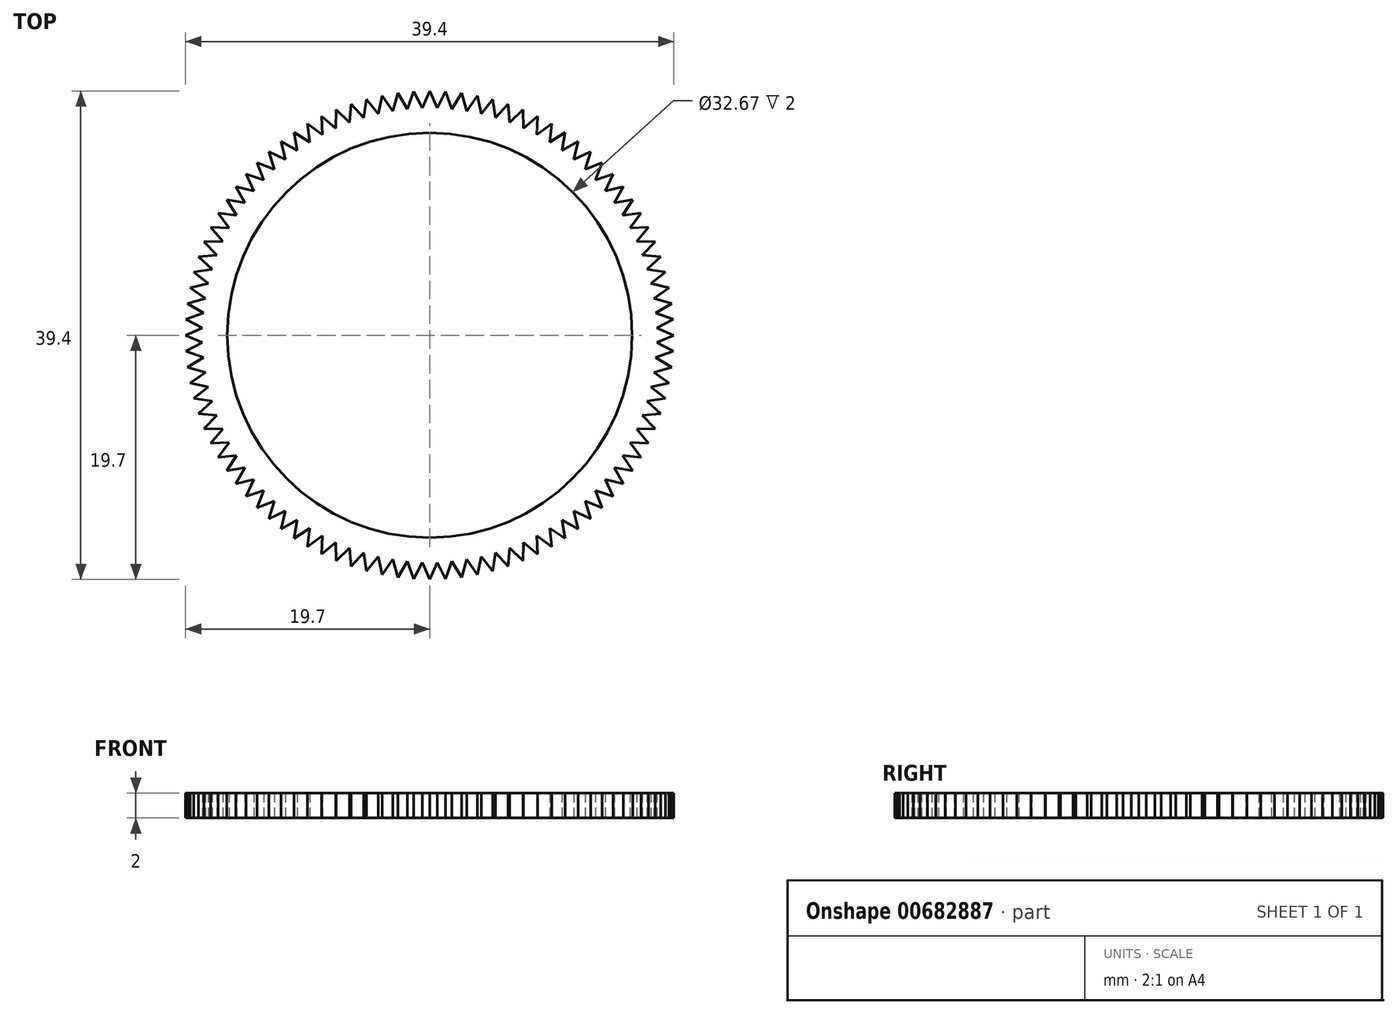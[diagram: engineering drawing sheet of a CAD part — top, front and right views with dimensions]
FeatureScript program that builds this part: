
annotation { "Feature Type Name" : "Feature", "Feature Type Description" : "" }
export const myFeature = defineFeature(function(context is Context, id is Id, definition is map)
    precondition{}
    {
        {
            var Q0;
            Q0=qCreatedBy(makeId("Top.planeOp"),FACE);
            var sketch = newSketch(context, id + "F0", { "sketchPlane" : qUnion([Q0])});
            skLineSegment(sketch, "E0", {"start": v(0, 19.7) * mm, "end": v(0.6, 18.33) * mm});
            skLineSegment(sketch, "E1.MirrorCS", {"start": v(0, 19.7) * mm, "end": v(-0.6, 18.33) * mm});
            skLineSegment(sketch, "E2.1.0", {"start": v(-1.29, 19.66) * mm, "end": v(-1.8, 18.25) * mm});
            skLineSegment(sketch, "E2.1.1", {"start": v(-1.29, 19.66) * mm, "end": v(-0.6, 18.33) * mm});
            skLineSegment(sketch, "E2.2.0", {"start": v(-2.57, 19.53) * mm, "end": v(-2.99, 18.1) * mm});
            skLineSegment(sketch, "E2.2.1", {"start": v(-2.57, 19.53) * mm, "end": v(-1.8, 18.25) * mm});
            skPoint(sketch, "E2.center", {"position": v(0, 0) * mm});
            skLineSegment(sketch, "E3.2.3.0", {"start": v(-3.84, 19.32) * mm, "end": v(-4.16, 17.86) * mm});
            skLineSegment(sketch, "E3.3.3.0", {"start": v(-3.84, 19.32) * mm, "end": v(-2.99, 18.1) * mm});
            skLineSegment(sketch, "E3.2.4.0", {"start": v(-5.1, 19.03) * mm, "end": v(-5.32, 17.55) * mm});
            skLineSegment(sketch, "E3.3.4.0", {"start": v(-5.1, 19.03) * mm, "end": v(-4.16, 17.86) * mm});
            skLineSegment(sketch, "E3.2.5.0", {"start": v(-6.33, 18.66) * mm, "end": v(-6.46, 17.16) * mm});
            skLineSegment(sketch, "E3.3.5.0", {"start": v(-6.33, 18.66) * mm, "end": v(-5.32, 17.55) * mm});
            skLineSegment(sketch, "E3.2.6.0", {"start": v(-7.54, 18.2) * mm, "end": v(-7.57, 16.7) * mm});
            skLineSegment(sketch, "E3.3.6.0", {"start": v(-7.54, 18.2) * mm, "end": v(-6.46, 17.16) * mm});
            skLineSegment(sketch, "E3.2.7.0", {"start": v(-8.71, 17.67) * mm, "end": v(-8.64, 16.17) * mm});
            skLineSegment(sketch, "E3.3.7.0", {"start": v(-8.71, 17.67) * mm, "end": v(-7.57, 16.7) * mm});
            skLineSegment(sketch, "E3.2.8.0", {"start": v(-9.85, 17.06) * mm, "end": v(-9.68, 15.57) * mm});
            skLineSegment(sketch, "E3.3.8.0", {"start": v(-9.85, 17.06) * mm, "end": v(-8.64, 16.17) * mm});
            skLineSegment(sketch, "E3.2.9.0", {"start": v(-10.95, 16.38) * mm, "end": v(-10.68, 14.9) * mm});
            skLineSegment(sketch, "E3.3.9.0", {"start": v(-10.95, 16.38) * mm, "end": v(-9.68, 15.57) * mm});
            skLineSegment(sketch, "E4.2.10.0", {"start": v(-12, 15.63) * mm, "end": v(-11.63, 14.18) * mm});
            skLineSegment(sketch, "E4.3.10.0", {"start": v(-12, 15.63) * mm, "end": v(-10.68, 14.9) * mm});
            skLineSegment(sketch, "E4.2.11.0", {"start": v(-13, 14.81) * mm, "end": v(-12.54, 13.38) * mm});
            skLineSegment(sketch, "E4.3.11.0", {"start": v(-13, 14.81) * mm, "end": v(-11.63, 14.18) * mm});
            skLineSegment(sketch, "E4.2.12.0", {"start": v(-13.93, 13.93) * mm, "end": v(-13.38, 12.54) * mm});
            skLineSegment(sketch, "E4.3.12.0", {"start": v(-13.93, 13.93) * mm, "end": v(-12.54, 13.38) * mm});
            skLineSegment(sketch, "E4.2.13.0", {"start": v(-14.81, 13) * mm, "end": v(-14.18, 11.63) * mm});
            skLineSegment(sketch, "E4.3.13.0", {"start": v(-14.81, 13) * mm, "end": v(-13.38, 12.54) * mm});
            skLineSegment(sketch, "E4.2.14.0", {"start": v(-15.63, 12) * mm, "end": v(-14.9, 10.68) * mm});
            skLineSegment(sketch, "E4.3.14.0", {"start": v(-15.63, 12) * mm, "end": v(-14.18, 11.63) * mm});
            skLineSegment(sketch, "E4.2.15.0", {"start": v(-16.38, 10.95) * mm, "end": v(-15.57, 9.68) * mm});
            skLineSegment(sketch, "E4.3.15.0", {"start": v(-16.38, 10.95) * mm, "end": v(-14.9, 10.68) * mm});
            skLineSegment(sketch, "E4.2.16.0", {"start": v(-17.06, 9.85) * mm, "end": v(-16.17, 8.64) * mm});
            skLineSegment(sketch, "E4.3.16.0", {"start": v(-17.06, 9.85) * mm, "end": v(-15.57, 9.68) * mm});
            skLineSegment(sketch, "E4.2.17.0", {"start": v(-17.67, 8.71) * mm, "end": v(-16.7, 7.57) * mm});
            skLineSegment(sketch, "E4.3.17.0", {"start": v(-17.67, 8.71) * mm, "end": v(-16.17, 8.64) * mm});
            skLineSegment(sketch, "E4.2.18.0", {"start": v(-18.2, 7.54) * mm, "end": v(-17.16, 6.46) * mm});
            skLineSegment(sketch, "E4.3.18.0", {"start": v(-18.2, 7.54) * mm, "end": v(-16.7, 7.57) * mm});
            skLineSegment(sketch, "E4.2.19.0", {"start": v(-18.66, 6.33) * mm, "end": v(-17.55, 5.32) * mm});
            skLineSegment(sketch, "E4.3.19.0", {"start": v(-18.66, 6.33) * mm, "end": v(-17.16, 6.46) * mm});
            skLineSegment(sketch, "E4.2.20.0", {"start": v(-19.03, 5.1) * mm, "end": v(-17.86, 4.16) * mm});
            skLineSegment(sketch, "E4.3.20.0", {"start": v(-19.03, 5.1) * mm, "end": v(-17.55, 5.32) * mm});
            skLineSegment(sketch, "E4.2.21.0", {"start": v(-19.32, 3.84) * mm, "end": v(-18.1, 2.99) * mm});
            skLineSegment(sketch, "E4.3.21.0", {"start": v(-19.32, 3.84) * mm, "end": v(-17.86, 4.16) * mm});
            skLineSegment(sketch, "E4.2.22.0", {"start": v(-19.53, 2.57) * mm, "end": v(-18.25, 1.8) * mm});
            skLineSegment(sketch, "E4.3.22.0", {"start": v(-19.53, 2.57) * mm, "end": v(-18.1, 2.99) * mm});
            skLineSegment(sketch, "E4.2.23.0", {"start": v(-19.66, 1.29) * mm, "end": v(-18.33, 0.6) * mm});
            skLineSegment(sketch, "E4.3.23.0", {"start": v(-19.66, 1.29) * mm, "end": v(-18.25, 1.8) * mm});
            skLineSegment(sketch, "E4.2.24.0", {"start": v(-19.7, 0) * mm, "end": v(-18.33, -0.6) * mm});
            skLineSegment(sketch, "E4.3.24.0", {"start": v(-19.7, 0) * mm, "end": v(-18.33, 0.6) * mm});
            skLineSegment(sketch, "E4.2.25.0", {"start": v(-19.66, -1.29) * mm, "end": v(-18.25, -1.8) * mm});
            skLineSegment(sketch, "E4.3.25.0", {"start": v(-19.66, -1.29) * mm, "end": v(-18.33, -0.6) * mm});
            skLineSegment(sketch, "E4.2.26.0", {"start": v(-19.53, -2.57) * mm, "end": v(-18.1, -2.99) * mm});
            skLineSegment(sketch, "E4.3.26.0", {"start": v(-19.53, -2.57) * mm, "end": v(-18.25, -1.8) * mm});
            skLineSegment(sketch, "E4.2.27.0", {"start": v(-19.32, -3.84) * mm, "end": v(-17.86, -4.16) * mm});
            skLineSegment(sketch, "E4.3.27.0", {"start": v(-19.32, -3.84) * mm, "end": v(-18.1, -2.99) * mm});
            skLineSegment(sketch, "E4.2.28.0", {"start": v(-19.03, -5.1) * mm, "end": v(-17.55, -5.32) * mm});
            skLineSegment(sketch, "E4.3.28.0", {"start": v(-19.03, -5.1) * mm, "end": v(-17.86, -4.16) * mm});
            skLineSegment(sketch, "E4.2.29.0", {"start": v(-18.66, -6.33) * mm, "end": v(-17.16, -6.46) * mm});
            skLineSegment(sketch, "E4.3.29.0", {"start": v(-18.66, -6.33) * mm, "end": v(-17.55, -5.32) * mm});
            skLineSegment(sketch, "E4.2.30.0", {"start": v(-18.2, -7.54) * mm, "end": v(-16.7, -7.57) * mm});
            skLineSegment(sketch, "E4.3.30.0", {"start": v(-18.2, -7.54) * mm, "end": v(-17.16, -6.46) * mm});
            skLineSegment(sketch, "E4.2.31.0", {"start": v(-17.67, -8.71) * mm, "end": v(-16.17, -8.64) * mm});
            skLineSegment(sketch, "E4.3.31.0", {"start": v(-17.67, -8.71) * mm, "end": v(-16.7, -7.57) * mm});
            skLineSegment(sketch, "E4.2.32.0", {"start": v(-17.06, -9.85) * mm, "end": v(-15.57, -9.68) * mm});
            skLineSegment(sketch, "E4.3.32.0", {"start": v(-17.06, -9.85) * mm, "end": v(-16.17, -8.64) * mm});
            skLineSegment(sketch, "E4.2.33.0", {"start": v(-16.38, -10.95) * mm, "end": v(-14.9, -10.68) * mm});
            skLineSegment(sketch, "E4.3.33.0", {"start": v(-16.38, -10.95) * mm, "end": v(-15.57, -9.68) * mm});
            skLineSegment(sketch, "E4.2.34.0", {"start": v(-15.63, -12) * mm, "end": v(-14.18, -11.63) * mm});
            skLineSegment(sketch, "E4.3.34.0", {"start": v(-15.63, -12) * mm, "end": v(-14.9, -10.68) * mm});
            skLineSegment(sketch, "E4.2.35.0", {"start": v(-14.81, -13) * mm, "end": v(-13.38, -12.54) * mm});
            skLineSegment(sketch, "E4.3.35.0", {"start": v(-14.81, -13) * mm, "end": v(-14.18, -11.63) * mm});
            skLineSegment(sketch, "E4.2.36.0", {"start": v(-13.93, -13.93) * mm, "end": v(-12.54, -13.38) * mm});
            skLineSegment(sketch, "E4.3.36.0", {"start": v(-13.93, -13.93) * mm, "end": v(-13.38, -12.54) * mm});
            skLineSegment(sketch, "E4.2.37.0", {"start": v(-13, -14.81) * mm, "end": v(-11.63, -14.18) * mm});
            skLineSegment(sketch, "E4.3.37.0", {"start": v(-13, -14.81) * mm, "end": v(-12.54, -13.38) * mm});
            skLineSegment(sketch, "E4.2.38.0", {"start": v(-12, -15.63) * mm, "end": v(-10.68, -14.9) * mm});
            skLineSegment(sketch, "E4.3.38.0", {"start": v(-12, -15.63) * mm, "end": v(-11.63, -14.18) * mm});
            skLineSegment(sketch, "E4.2.39.0", {"start": v(-10.95, -16.38) * mm, "end": v(-9.68, -15.57) * mm});
            skLineSegment(sketch, "E4.3.39.0", {"start": v(-10.95, -16.38) * mm, "end": v(-10.68, -14.9) * mm});
            skLineSegment(sketch, "E4.2.40.0", {"start": v(-9.85, -17.06) * mm, "end": v(-8.64, -16.17) * mm});
            skLineSegment(sketch, "E4.3.40.0", {"start": v(-9.85, -17.06) * mm, "end": v(-9.68, -15.57) * mm});
            skLineSegment(sketch, "E4.2.41.0", {"start": v(-8.71, -17.67) * mm, "end": v(-7.57, -16.7) * mm});
            skLineSegment(sketch, "E4.3.41.0", {"start": v(-8.71, -17.67) * mm, "end": v(-8.64, -16.17) * mm});
            skLineSegment(sketch, "E4.2.42.0", {"start": v(-7.54, -18.2) * mm, "end": v(-6.46, -17.16) * mm});
            skLineSegment(sketch, "E4.3.42.0", {"start": v(-7.54, -18.2) * mm, "end": v(-7.57, -16.7) * mm});
            skLineSegment(sketch, "E4.2.43.0", {"start": v(-6.33, -18.66) * mm, "end": v(-5.32, -17.55) * mm});
            skLineSegment(sketch, "E4.3.43.0", {"start": v(-6.33, -18.66) * mm, "end": v(-6.46, -17.16) * mm});
            skLineSegment(sketch, "E4.2.44.0", {"start": v(-5.1, -19.03) * mm, "end": v(-4.16, -17.86) * mm});
            skLineSegment(sketch, "E4.3.44.0", {"start": v(-5.1, -19.03) * mm, "end": v(-5.32, -17.55) * mm});
            skLineSegment(sketch, "E4.2.45.0", {"start": v(-3.84, -19.32) * mm, "end": v(-2.99, -18.1) * mm});
            skLineSegment(sketch, "E4.3.45.0", {"start": v(-3.84, -19.32) * mm, "end": v(-4.16, -17.86) * mm});
            skLineSegment(sketch, "E4.2.46.0", {"start": v(-2.57, -19.53) * mm, "end": v(-1.8, -18.25) * mm});
            skLineSegment(sketch, "E4.3.46.0", {"start": v(-2.57, -19.53) * mm, "end": v(-2.99, -18.1) * mm});
            skLineSegment(sketch, "E4.2.47.0", {"start": v(-1.29, -19.66) * mm, "end": v(-0.6, -18.33) * mm});
            skLineSegment(sketch, "E4.3.47.0", {"start": v(-1.29, -19.66) * mm, "end": v(-1.8, -18.25) * mm});
            skLineSegment(sketch, "E4.2.48.0", {"start": v(0, -19.7) * mm, "end": v(0.6, -18.33) * mm});
            skLineSegment(sketch, "E4.3.48.0", {"start": v(0, -19.7) * mm, "end": v(-0.6, -18.33) * mm});
            skLineSegment(sketch, "E4.2.49.0", {"start": v(1.29, -19.66) * mm, "end": v(1.8, -18.25) * mm});
            skLineSegment(sketch, "E4.3.49.0", {"start": v(1.29, -19.66) * mm, "end": v(0.6, -18.33) * mm});
            skLineSegment(sketch, "E4.2.50.0", {"start": v(2.57, -19.53) * mm, "end": v(2.99, -18.1) * mm});
            skLineSegment(sketch, "E4.3.50.0", {"start": v(2.57, -19.53) * mm, "end": v(1.8, -18.25) * mm});
            skLineSegment(sketch, "E4.2.51.0", {"start": v(3.84, -19.32) * mm, "end": v(4.16, -17.86) * mm});
            skLineSegment(sketch, "E4.3.51.0", {"start": v(3.84, -19.32) * mm, "end": v(2.99, -18.1) * mm});
            skLineSegment(sketch, "E4.2.52.0", {"start": v(5.1, -19.03) * mm, "end": v(5.32, -17.55) * mm});
            skLineSegment(sketch, "E4.3.52.0", {"start": v(5.1, -19.03) * mm, "end": v(4.16, -17.86) * mm});
            skLineSegment(sketch, "E4.2.53.0", {"start": v(6.33, -18.66) * mm, "end": v(6.46, -17.16) * mm});
            skLineSegment(sketch, "E4.3.53.0", {"start": v(6.33, -18.66) * mm, "end": v(5.32, -17.55) * mm});
            skLineSegment(sketch, "E4.2.54.0", {"start": v(7.54, -18.2) * mm, "end": v(7.57, -16.7) * mm});
            skLineSegment(sketch, "E4.3.54.0", {"start": v(7.54, -18.2) * mm, "end": v(6.46, -17.16) * mm});
            skLineSegment(sketch, "E4.2.55.0", {"start": v(8.71, -17.67) * mm, "end": v(8.64, -16.17) * mm});
            skLineSegment(sketch, "E4.3.55.0", {"start": v(8.71, -17.67) * mm, "end": v(7.57, -16.7) * mm});
            skLineSegment(sketch, "E4.2.56.0", {"start": v(9.85, -17.06) * mm, "end": v(9.68, -15.57) * mm});
            skLineSegment(sketch, "E4.3.56.0", {"start": v(9.85, -17.06) * mm, "end": v(8.64, -16.17) * mm});
            skLineSegment(sketch, "E4.2.57.0", {"start": v(10.95, -16.38) * mm, "end": v(10.68, -14.9) * mm});
            skLineSegment(sketch, "E4.3.57.0", {"start": v(10.95, -16.38) * mm, "end": v(9.68, -15.57) * mm});
            skLineSegment(sketch, "E4.2.58.0", {"start": v(12, -15.63) * mm, "end": v(11.63, -14.18) * mm});
            skLineSegment(sketch, "E4.3.58.0", {"start": v(12, -15.63) * mm, "end": v(10.68, -14.9) * mm});
            skLineSegment(sketch, "E4.2.59.0", {"start": v(13, -14.81) * mm, "end": v(12.54, -13.38) * mm});
            skLineSegment(sketch, "E4.3.59.0", {"start": v(13, -14.81) * mm, "end": v(11.63, -14.18) * mm});
            skLineSegment(sketch, "E4.2.60.0", {"start": v(13.93, -13.93) * mm, "end": v(13.38, -12.54) * mm});
            skLineSegment(sketch, "E4.3.60.0", {"start": v(13.93, -13.93) * mm, "end": v(12.54, -13.38) * mm});
            skLineSegment(sketch, "E4.2.61.0", {"start": v(14.81, -13) * mm, "end": v(14.18, -11.63) * mm});
            skLineSegment(sketch, "E4.3.61.0", {"start": v(14.81, -13) * mm, "end": v(13.38, -12.54) * mm});
            skLineSegment(sketch, "E4.2.62.0", {"start": v(15.63, -12) * mm, "end": v(14.9, -10.68) * mm});
            skLineSegment(sketch, "E4.3.62.0", {"start": v(15.63, -12) * mm, "end": v(14.18, -11.63) * mm});
            skLineSegment(sketch, "E4.2.63.0", {"start": v(16.38, -10.95) * mm, "end": v(15.57, -9.68) * mm});
            skLineSegment(sketch, "E4.3.63.0", {"start": v(16.38, -10.95) * mm, "end": v(14.9, -10.68) * mm});
            skLineSegment(sketch, "E4.2.64.0", {"start": v(17.06, -9.85) * mm, "end": v(16.17, -8.64) * mm});
            skLineSegment(sketch, "E4.3.64.0", {"start": v(17.06, -9.85) * mm, "end": v(15.57, -9.68) * mm});
            skLineSegment(sketch, "E4.2.65.0", {"start": v(17.67, -8.71) * mm, "end": v(16.7, -7.57) * mm});
            skLineSegment(sketch, "E4.3.65.0", {"start": v(17.67, -8.71) * mm, "end": v(16.17, -8.64) * mm});
            skLineSegment(sketch, "E4.2.66.0", {"start": v(18.2, -7.54) * mm, "end": v(17.16, -6.46) * mm});
            skLineSegment(sketch, "E4.3.66.0", {"start": v(18.2, -7.54) * mm, "end": v(16.7, -7.57) * mm});
            skLineSegment(sketch, "E4.2.67.0", {"start": v(18.66, -6.33) * mm, "end": v(17.55, -5.32) * mm});
            skLineSegment(sketch, "E4.3.67.0", {"start": v(18.66, -6.33) * mm, "end": v(17.16, -6.46) * mm});
            skLineSegment(sketch, "E4.2.68.0", {"start": v(19.03, -5.1) * mm, "end": v(17.86, -4.16) * mm});
            skLineSegment(sketch, "E4.3.68.0", {"start": v(19.03, -5.1) * mm, "end": v(17.55, -5.32) * mm});
            skLineSegment(sketch, "E4.2.69.0", {"start": v(19.32, -3.84) * mm, "end": v(18.1, -2.99) * mm});
            skLineSegment(sketch, "E4.3.69.0", {"start": v(19.32, -3.84) * mm, "end": v(17.86, -4.16) * mm});
            skLineSegment(sketch, "E4.2.70.0", {"start": v(19.53, -2.57) * mm, "end": v(18.25, -1.8) * mm});
            skLineSegment(sketch, "E4.3.70.0", {"start": v(19.53, -2.57) * mm, "end": v(18.1, -2.99) * mm});
            skLineSegment(sketch, "E4.2.71.0", {"start": v(19.66, -1.29) * mm, "end": v(18.33, -0.6) * mm});
            skLineSegment(sketch, "E4.3.71.0", {"start": v(19.66, -1.29) * mm, "end": v(18.25, -1.8) * mm});
            skLineSegment(sketch, "E4.2.72.0", {"start": v(19.7, 0) * mm, "end": v(18.33, 0.6) * mm});
            skLineSegment(sketch, "E4.3.72.0", {"start": v(19.7, 0) * mm, "end": v(18.33, -0.6) * mm});
            skLineSegment(sketch, "E4.2.73.0", {"start": v(19.66, 1.29) * mm, "end": v(18.25, 1.8) * mm});
            skLineSegment(sketch, "E4.3.73.0", {"start": v(19.66, 1.29) * mm, "end": v(18.33, 0.6) * mm});
            skLineSegment(sketch, "E4.2.74.0", {"start": v(19.53, 2.57) * mm, "end": v(18.1, 2.99) * mm});
            skLineSegment(sketch, "E4.3.74.0", {"start": v(19.53, 2.57) * mm, "end": v(18.25, 1.8) * mm});
            skLineSegment(sketch, "E4.2.75.0", {"start": v(19.32, 3.84) * mm, "end": v(17.86, 4.16) * mm});
            skLineSegment(sketch, "E4.3.75.0", {"start": v(19.32, 3.84) * mm, "end": v(18.1, 2.99) * mm});
            skLineSegment(sketch, "E4.2.76.0", {"start": v(19.03, 5.1) * mm, "end": v(17.55, 5.32) * mm});
            skLineSegment(sketch, "E4.3.76.0", {"start": v(19.03, 5.1) * mm, "end": v(17.86, 4.16) * mm});
            skLineSegment(sketch, "E4.2.77.0", {"start": v(18.66, 6.33) * mm, "end": v(17.16, 6.46) * mm});
            skLineSegment(sketch, "E4.3.77.0", {"start": v(18.66, 6.33) * mm, "end": v(17.55, 5.32) * mm});
            skLineSegment(sketch, "E4.2.78.0", {"start": v(18.2, 7.54) * mm, "end": v(16.7, 7.57) * mm});
            skLineSegment(sketch, "E4.3.78.0", {"start": v(18.2, 7.54) * mm, "end": v(17.16, 6.46) * mm});
            skLineSegment(sketch, "E4.2.79.0", {"start": v(17.67, 8.71) * mm, "end": v(16.17, 8.64) * mm});
            skLineSegment(sketch, "E4.3.79.0", {"start": v(17.67, 8.71) * mm, "end": v(16.7, 7.57) * mm});
            skLineSegment(sketch, "E4.2.80.0", {"start": v(17.06, 9.85) * mm, "end": v(15.57, 9.68) * mm});
            skLineSegment(sketch, "E4.3.80.0", {"start": v(17.06, 9.85) * mm, "end": v(16.17, 8.64) * mm});
            skLineSegment(sketch, "E4.2.81.0", {"start": v(16.38, 10.95) * mm, "end": v(14.9, 10.68) * mm});
            skLineSegment(sketch, "E4.3.81.0", {"start": v(16.38, 10.95) * mm, "end": v(15.57, 9.68) * mm});
            skLineSegment(sketch, "E4.2.82.0", {"start": v(15.63, 12) * mm, "end": v(14.18, 11.63) * mm});
            skLineSegment(sketch, "E4.3.82.0", {"start": v(15.63, 12) * mm, "end": v(14.9, 10.68) * mm});
            skLineSegment(sketch, "E4.2.83.0", {"start": v(14.81, 13) * mm, "end": v(13.38, 12.54) * mm});
            skLineSegment(sketch, "E4.3.83.0", {"start": v(14.81, 13) * mm, "end": v(14.18, 11.63) * mm});
            skLineSegment(sketch, "E4.2.84.0", {"start": v(13.93, 13.93) * mm, "end": v(12.54, 13.38) * mm});
            skLineSegment(sketch, "E4.3.84.0", {"start": v(13.93, 13.93) * mm, "end": v(13.38, 12.54) * mm});
            skLineSegment(sketch, "E4.2.85.0", {"start": v(13, 14.81) * mm, "end": v(11.63, 14.18) * mm});
            skLineSegment(sketch, "E4.3.85.0", {"start": v(13, 14.81) * mm, "end": v(12.54, 13.38) * mm});
            skLineSegment(sketch, "E4.2.86.0", {"start": v(12, 15.63) * mm, "end": v(10.68, 14.9) * mm});
            skLineSegment(sketch, "E4.3.86.0", {"start": v(12, 15.63) * mm, "end": v(11.63, 14.18) * mm});
            skLineSegment(sketch, "E4.2.87.0", {"start": v(10.95, 16.38) * mm, "end": v(9.68, 15.57) * mm});
            skLineSegment(sketch, "E4.3.87.0", {"start": v(10.95, 16.38) * mm, "end": v(10.68, 14.9) * mm});
            skLineSegment(sketch, "E4.2.88.0", {"start": v(9.85, 17.06) * mm, "end": v(8.64, 16.17) * mm});
            skLineSegment(sketch, "E4.3.88.0", {"start": v(9.85, 17.06) * mm, "end": v(9.68, 15.57) * mm});
            skLineSegment(sketch, "E4.2.89.0", {"start": v(8.71, 17.67) * mm, "end": v(7.57, 16.7) * mm});
            skLineSegment(sketch, "E4.3.89.0", {"start": v(8.71, 17.67) * mm, "end": v(8.64, 16.17) * mm});
            skLineSegment(sketch, "E4.2.90.0", {"start": v(7.54, 18.2) * mm, "end": v(6.46, 17.16) * mm});
            skLineSegment(sketch, "E4.3.90.0", {"start": v(7.54, 18.2) * mm, "end": v(7.57, 16.7) * mm});
            skLineSegment(sketch, "E4.2.91.0", {"start": v(6.33, 18.66) * mm, "end": v(5.32, 17.55) * mm});
            skLineSegment(sketch, "E4.3.91.0", {"start": v(6.33, 18.66) * mm, "end": v(6.46, 17.16) * mm});
            skLineSegment(sketch, "E4.2.92.0", {"start": v(5.1, 19.03) * mm, "end": v(4.16, 17.86) * mm});
            skLineSegment(sketch, "E4.3.92.0", {"start": v(5.1, 19.03) * mm, "end": v(5.32, 17.55) * mm});
            skLineSegment(sketch, "E4.2.93.0", {"start": v(3.84, 19.32) * mm, "end": v(2.99, 18.1) * mm});
            skLineSegment(sketch, "E4.3.93.0", {"start": v(3.84, 19.32) * mm, "end": v(4.16, 17.86) * mm});
            skLineSegment(sketch, "E4.2.94.0", {"start": v(2.57, 19.53) * mm, "end": v(1.8, 18.25) * mm});
            skLineSegment(sketch, "E4.3.94.0", {"start": v(2.57, 19.53) * mm, "end": v(2.99, 18.1) * mm});
            skLineSegment(sketch, "E4.2.95.0", {"start": v(1.29, 19.66) * mm, "end": v(0.6, 18.33) * mm});
            skLineSegment(sketch, "E4.3.95.0", {"start": v(1.29, 19.66) * mm, "end": v(1.8, 18.25) * mm});
            skCircle(sketch, "E5", {"center": v(0, 0) * mm, "radius": 16.34 * mm});
            skSolve(sketch);
        }
        {
            var Q0;
            Q0=makeQuery(id+"F0.imprint","IMPRINT",FACE,{"disambiguationData":[TD([[makeQuery(id+"F0.imprint","IMPRINT",EDGE,{"derivedFrom":sQuery(id+"F0.wireOp",EDGE,"E0")}),-1.0]])]});
            extrude(context, id + "F1", {"entities" : qUnion([Q0]), "depth" : 2 * mm, "offsetDistance" : 25 * mm});
        }
    });
